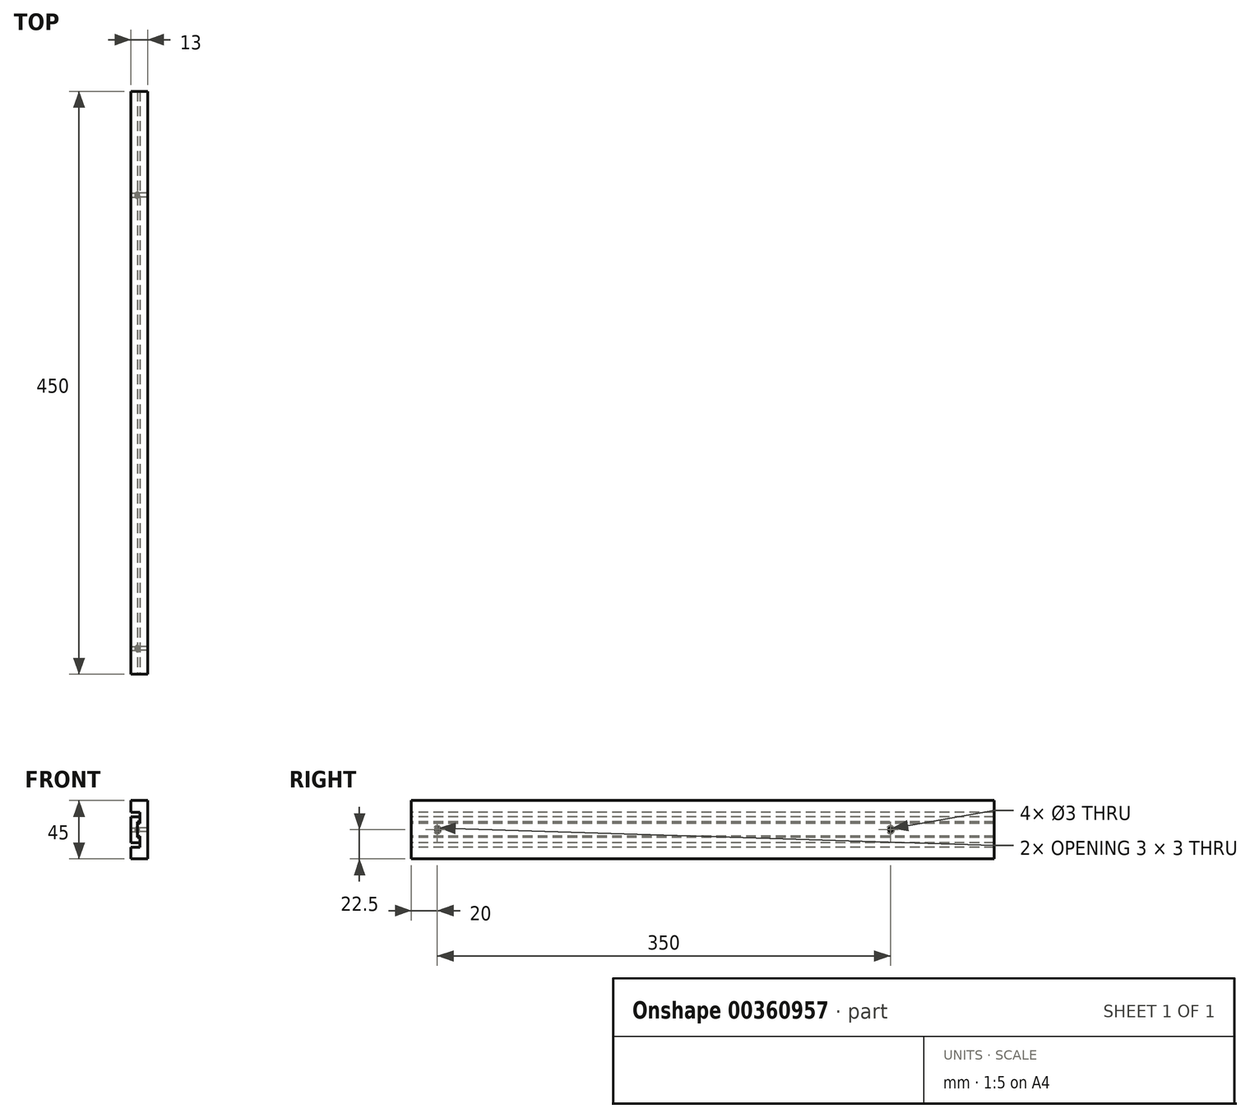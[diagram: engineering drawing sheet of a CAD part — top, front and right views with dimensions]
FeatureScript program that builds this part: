
annotation { "Feature Type Name" : "Feature", "Feature Type Description" : "" }
export const myFeature = defineFeature(function(context is Context, id is Id, definition is map)
    precondition{}
    {
        {
            var Q0;
            Q0=qCreatedBy(makeId("Front.planeOp"),FACE);
            var sketch = newSketch(context, id + "F0", { "sketchPlane" : qUnion([Q0])});
            skLineSegment(sketch, "E0.bottom", {"start": v(-7, 10) * mm, "end": v(0, 10) * mm});
            skLineSegment(sketch, "E0.top", {"start": v(-7, -10) * mm, "end": v(0, -10) * mm});
            skLineSegment(sketch, "E0.left", {"start": v(-7, 10) * mm, "end": v(-7, -10) * mm});
            skLineSegment(sketch, "E0.right", {"start": v(0, 10) * mm, "end": v(0, 6) * mm});
            skLineSegment(sketch, "E1", {"start": v(0, 6) * mm, "end": v(-2, 6) * mm});
            skLineSegment(sketch, "E2", {"start": v(-2, 6) * mm, "end": v(-2, -6) * mm});
            skLineSegment(sketch, "E3", {"start": v(-2, -6) * mm, "end": v(0, -6) * mm});
            skLineSegment(sketch, "E4.trimOffspring", {"start": v(0, -6) * mm, "end": v(0, -10) * mm});
            skSolve(sketch);
        }
        {
            var Q0;
            Q0=makeQuery(id+"F0.imprint","IMPRINT",FACE,{"disambiguationData":[TD([[makeQuery(id+"F0.imprint","IMPRINT",EDGE,{"derivedFrom":sQuery(id+"F0.wireOp",EDGE,"E0.bottom")}),-1.0]])]});
            extrude(context, id + "F1", {"entities" : qUnion([Q0]), "oppositeDirection" : true, "depth" : 450 * mm});
        }
        {
            var Q0;
            Q0=makeQuery(id+"F1.opExtrude","SWEPT_FACE",FACE,{"disambiguationData":[OSD([sQuery(id+"F0.wireOp",EDGE,"E2")])]});
            var sketch = newSketch(context, id + "F2", { "sketchPlane" : qUnion([Q0])});
            skPoint(sketch, "E5", {"position": v(20, 0) * mm});
            skPoint(sketch, "E6", {"position": v(370, 0) * mm});
            skSolve(sketch);
        }
        {
            var Q0;
            Q0=sQuery(id+"F2.wireOp",VERTEX,"E5");
            var Q1;
            Q1=sQuery(id+"F2.wireOp",VERTEX,"E6");
            var Q2;
            Q2=makeQuery(id+"F1.opExtrude","SWEPT_BODY",BODY,{"disambiguationData":[OSD([sQuery(id+"F0.wireOp",EDGE,"E0.bottom"),sQuery(id+"F0.wireOp",EDGE,"E0.top"),sQuery(id+"F0.wireOp",EDGE,"E0.left"),sQuery(id+"F0.wireOp",EDGE,"E0.right"),sQuery(id+"F0.wireOp",EDGE,"E1"),sQuery(id+"F0.wireOp",EDGE,"E2"),sQuery(id+"F0.wireOp",EDGE,"E3"),sQuery(id+"F0.wireOp",EDGE,"E4.trimOffspring")])]});
            hole(context, id + "F3", {"style" : HoleStyle.C_SINK, "endStyle" : HoleEndStyle.THROUGH, "holeDiameter" : 3 * mm, "cSinkDiameter" : 6 * mm, "cSinkAngle" : 90 * degree, "isTappedThrough" : true, "tappedDepth" : 12 * mm, "tapClearance" : 3, "locations" : qUnion([Q0, Q1]), "scope" : qUnion([Q2])});
        }
        {
            var Q0;
            Q0=qCreatedBy(makeId("Front.planeOp"),FACE);
            var sketch = newSketch(context, id + "F4", { "sketchPlane" : qUnion([Q0])});
            skLineSegment(sketch, "E7", {"start": v(-7, 22.5) * mm, "end": v(-7, 13.5) * mm});
            skLineSegment(sketch, "E8", {"start": v(-7, 13.5) * mm, "end": v(0, 13.5) * mm});
            skLineSegment(sketch, "E9", {"start": v(0, 13.5) * mm, "end": v(0, 5) * mm});
            skLineSegment(sketch, "E10", {"start": v(0, 5) * mm, "end": v(-2, 5) * mm});
            skLineSegment(sketch, "E11", {"start": v(-2, 5) * mm, "end": v(-2, -5) * mm});
            skLineSegment(sketch, "E12", {"start": v(-2, -5) * mm, "end": v(0, -5) * mm});
            skLineSegment(sketch, "E13", {"start": v(0, -5) * mm, "end": v(0, -13.5) * mm});
            skLineSegment(sketch, "E14", {"start": v(0, -13.5) * mm, "end": v(-7, -13.5) * mm});
            skLineSegment(sketch, "E15", {"start": v(-7, -13.5) * mm, "end": v(-7, -22.5) * mm});
            skLineSegment(sketch, "E16", {"start": v(-7, -22.5) * mm, "end": v(6, -22.5) * mm});
            skLineSegment(sketch, "E17", {"start": v(6, -22.5) * mm, "end": v(6, 22.5) * mm});
            skLineSegment(sketch, "E18", {"start": v(6, 22.5) * mm, "end": v(-7, 22.5) * mm});
            skSolve(sketch);
        }
        {
            var Q0;
            Q0=makeQuery(id+"F4.imprint","IMPRINT",FACE,{"disambiguationData":[TD([[makeQuery(id+"F4.imprint","IMPRINT",EDGE,{"derivedFrom":sQuery(id+"F4.wireOp",EDGE,"E7")}),1.0]])]});
            extrude(context, id + "F5", {"entities" : qUnion([Q0]), "oppositeDirection" : true, "depth" : 450 * mm});
        }
        {
            var Q0;
            Q0=makeQuery(id+"F5.opExtrude","SWEPT_FACE",FACE,{"disambiguationData":[OSD([sQuery(id+"F4.wireOp",EDGE,"E11")])]});
            var sketch = newSketch(context, id + "F6", { "sketchPlane" : qUnion([Q0])});
            skPoint(sketch, "E19", {"position": v(-20, 0) * mm});
            skPoint(sketch, "E20", {"position": v(-370, 0) * mm});
            skSolve(sketch);
        }
        {
            var Q0;
            Q0=sQuery(id+"F6.wireOp",VERTEX,"E19");
            var Q1;
            Q1=sQuery(id+"F6.wireOp",VERTEX,"E20");
            var Q2;
            Q2=makeQuery(id+"F5.opExtrude","SWEPT_BODY",BODY,{"disambiguationData":[OSD([sQuery(id+"F4.wireOp",EDGE,"E7"),sQuery(id+"F4.wireOp",EDGE,"E8"),sQuery(id+"F4.wireOp",EDGE,"E9"),sQuery(id+"F4.wireOp",EDGE,"E10"),sQuery(id+"F4.wireOp",EDGE,"E11"),sQuery(id+"F4.wireOp",EDGE,"E12"),sQuery(id+"F4.wireOp",EDGE,"E13"),sQuery(id+"F4.wireOp",EDGE,"E14"),sQuery(id+"F4.wireOp",EDGE,"E15"),sQuery(id+"F4.wireOp",EDGE,"E16"),sQuery(id+"F4.wireOp",EDGE,"E17"),sQuery(id+"F4.wireOp",EDGE,"E18")])]});
            hole(context, id + "F7", {"style" : HoleStyle.C_SINK, "endStyle" : HoleEndStyle.THROUGH, "holeDiameter" : 3 * mm, "cSinkDiameter" : 6 * mm, "cSinkAngle" : 90 * degree, "isTappedThrough" : true, "tappedDepth" : 12 * mm, "tapClearance" : 3, "locations" : qUnion([Q0, Q1]), "scope" : qUnion([Q2])});
        }
    });
